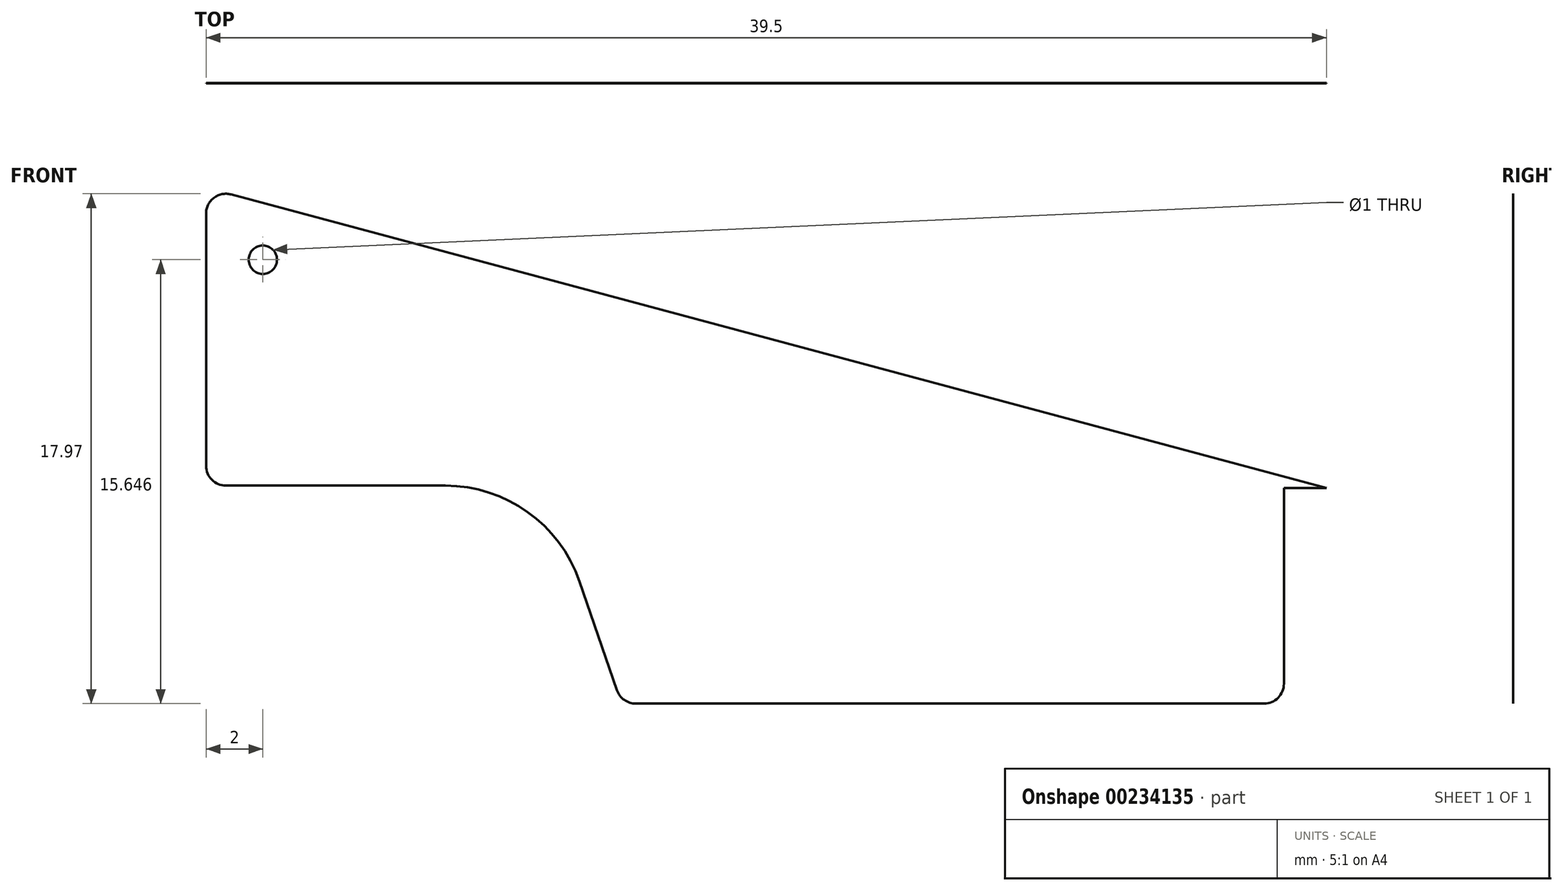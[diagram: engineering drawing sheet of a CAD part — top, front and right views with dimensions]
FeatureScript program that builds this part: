
annotation { "Feature Type Name" : "Feature", "Feature Type Description" : "" }
export const myFeature = defineFeature(function(context is Context, id is Id, definition is map)
    precondition{}
    {
        {
            var Q0;
            Q0=qCreatedBy(makeId("Front.planeOp"),FACE);
            var sketch = newSketch(context, id + "F0", { "sketchPlane" : qUnion([Q0])});
            skLineSegment(sketch, "E0", {"start": v(0.5, 0) * mm, "end": v(22.65, 0) * mm});
            skLineSegment(sketch, "E1", {"start": v(23.35, 0.7) * mm, "end": v(23.35, 7.6) * mm});
            skLineSegment(sketch, "E2", {"start": v(23.35, 7.6) * mm, "end": v(24.85, 7.6) * mm});
            skLineSegment(sketch, "E3", {"start": v(24.85, 7.6) * mm, "end": v(-13.77, 17.95) * mm});
            skLineSegment(sketch, "E4", {"start": v(-14.65, 17.27) * mm, "end": v(-14.65, 8.38) * mm});
            skLineSegment(sketch, "E5", {"start": v(-13.95, 7.68) * mm, "end": v(-6.21, 7.68) * mm});
            skLineSegment(sketch, "E6", {"start": v(-1.49, 4.31) * mm, "end": v(-0.16, 0.47) * mm});
            skPoint(sketch, "E7", {"position": v(-8.65, 7.68) * mm});
            skPoint(sketch, "E8.visualSharp", {"position": v(-2.65, 7.68) * mm});
            skArc(sketch, "E8.filletArc", {"start": v(-1.49, 4.31) * mm, "mid": v(-3.31, 6.75) * mm, "end": v(-6.21, 7.68) * mm});
            skPoint(sketch, "E9.visualSharp", {"position": v(-14.65, 18.18) * mm});
            skArc(sketch, "E9.filletArc", {"start": v(-13.77, 17.95) * mm, "mid": v(-14.38, 17.83) * mm, "end": v(-14.65, 17.27) * mm});
            skPoint(sketch, "E10.visualSharp", {"position": v(-14.65, 7.68) * mm});
            skArc(sketch, "E10.filletArc", {"start": v(-14.65, 8.38) * mm, "mid": v(-14.44, 7.89) * mm, "end": v(-13.95, 7.68) * mm});
            skPoint(sketch, "E11.visualSharp", {"position": v(0, 0) * mm});
            skArc(sketch, "E11.filletArc", {"start": v(-0.16, 0.47) * mm, "mid": v(0.1, 0.13) * mm, "end": v(0.5, 0) * mm});
            skPoint(sketch, "E12.visualSharp", {"position": v(23.35, 0) * mm});
            skArc(sketch, "E12.filletArc", {"start": v(22.65, 0) * mm, "mid": v(23.14, 0.2) * mm, "end": v(23.35, 0.7) * mm});
            skLineSegment(sketch, "E13", {"start": v(-12.65, 7.68) * mm, "end": v(-12.65, 17.65) * mm});
            skCircle(sketch, "E14", {"center": v(-12.65, 15.65) * mm, "radius": 0.5 * mm});
            skLineSegment(sketch, "E15", {"start": v(23.35, 7.6) * mm, "end": v(23.35, 8) * mm});
            skSolve(sketch);
        }
        {
            var Q0;
            Q0=makeQuery(id+"F0.imprint","IMPRINT",FACE,{"disambiguationData":[TD([[makeQuery(id+"F0.imprint","IMPRINT",EDGE,{"derivedFrom":sQuery(id+"F0.wireOp",EDGE,"E0")}),1.0]])]});
            var Q1;
            Q1=makeQuery(id+"F0.imprint","IMPRINT",FACE,{"disambiguationData":[TD([[makeQuery(id+"F0.imprint","IMPRINT",EDGE,{"derivedFrom":sQuery(id+"F0.wireOp",EDGE,"E4")}),1.0]])]});
            var Q2;
            {var subQ0=sQuery(id+"F0.wireOp",EDGE,"E2");Q2=makeQuery(id+"F0.imprint","IMPRINT",FACE,{"disambiguationData":[TD([[makeQuery(id+"F0.imprint","IMPRINT",EDGE,{"derivedFrom":subQ0}),1.0]])]});}
            extrude(context, id + "F1", {"entities" : qUnion([Q0, Q1, Q2]), "depth" : 1 / 406.4 * mm});
        }
    });
